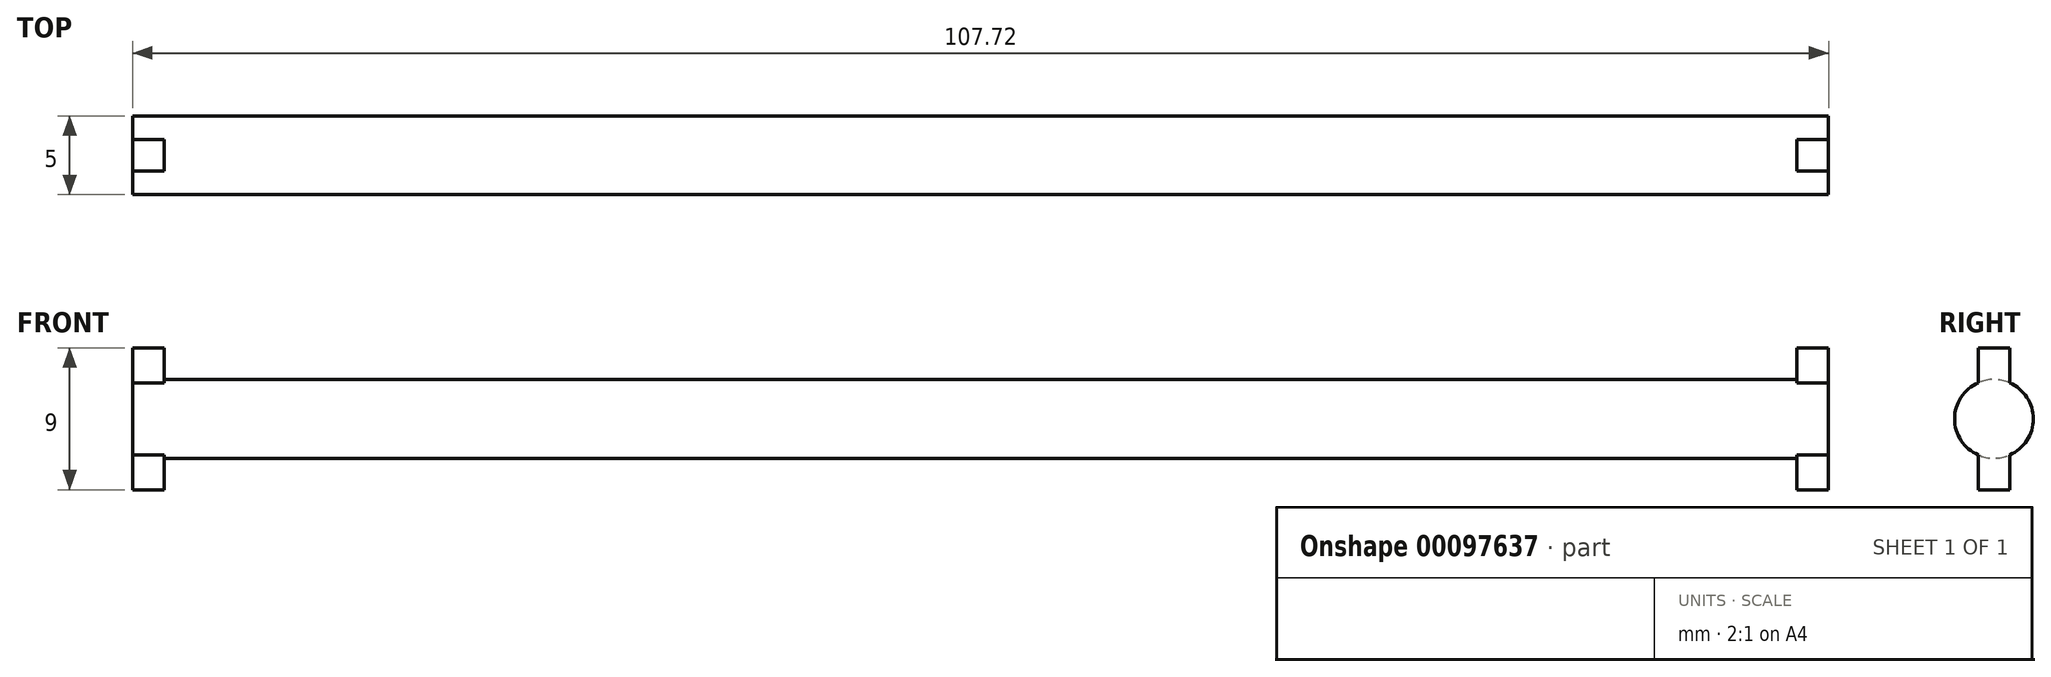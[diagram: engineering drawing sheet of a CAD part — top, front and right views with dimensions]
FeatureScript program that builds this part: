
annotation { "Feature Type Name" : "Feature", "Feature Type Description" : "" }
export const myFeature = defineFeature(function(context is Context, id is Id, definition is map)
    precondition{}
    {
        {
            var Q0;
            Q0=qCreatedBy(makeId("Right.planeOp"),FACE);
            var sketch = newSketch(context, id + "F0", { "sketchPlane" : qUnion([Q0])});
            skCircle(sketch, "E0", {"center": v(0, 0) * mm, "radius": 2.5 * mm});
            skSolve(sketch);
        }
        {
            var Q0;
            Q0=makeQuery(id+"F0.imprint","IMPRINT",FACE,{"disambiguationData":[TD([[makeQuery(id+"F0.imprint","IMPRINT",EDGE,{"derivedFrom":sQuery(id+"F0.wireOp",EDGE,"E0")}),1.0]])]});
            var Q1;
            Q1=sQuery(id+"F0.wireOp",EDGE,"E0");
            extrude(context, id + "F1", {"entities" : qUnion([Q0]), "surfaceEntities" : qUnion([Q1]), "endBound" : BoundingType.SYMMETRIC, "depth" : 107.7 * mm});
        }
        {
            var Q0;
            Q0=makeQuery(id+"F1.opExtrude","CAP_FACE",FACE,{"disambiguationData":[OSD([sQuery(id+"F0.wireOp",EDGE,"E0")])],"isStart":true});
            var sketch = newSketch(context, id + "F2", { "sketchPlane" : qUnion([Q0])});
            skLineSegment(sketch, "E1.bottom", {"start": v(1, -4.5) * mm, "end": v(-1, -4.5) * mm});
            skLineSegment(sketch, "E1.top", {"start": v(1, 4.5) * mm, "end": v(-1, 4.5) * mm});
            skLineSegment(sketch, "E1.left", {"start": v(1, -4.5) * mm, "end": v(1, 4.5) * mm});
            skLineSegment(sketch, "E1.right", {"start": v(-1, -4.5) * mm, "end": v(-1, 4.5) * mm});
            skPoint(sketch, "E1.middle", {"position": v(0, 0) * mm});
            skSolve(sketch);
        }
        {
            var Q0;
            {var subQ0=sQuery(id+"F2.wireOp",EDGE,"E1.top");Q0=makeQuery(id+"F2.imprint","IMPRINT",FACE,{"disambiguationData":[TD([[makeQuery(id+"F2.imprint","IMPRINT",EDGE,{"derivedFrom":subQ0}),1.0]])]});}
            var Q1;
            {var subQ0=sQuery(id+"F2.wireOp",EDGE,"E1.bottom");Q1=makeQuery(id+"F2.imprint","IMPRINT",FACE,{"disambiguationData":[TD([[makeQuery(id+"F2.imprint","IMPRINT",EDGE,{"derivedFrom":subQ0}),-1.0]])]});}
            extrude(context, id + "F3", {"entities" : qUnion([Q0, Q1]), "operationType" : NewBodyOperationType.ADD, "oppositeDirection" : true, "depth" : 2 * mm});
        }
        {
            var Q0;
            Q0=makeQuery(id+"F1.opExtrude","SWEPT_BODY",BODY,{"disambiguationData":[OSD([sQuery(id+"F0.wireOp",EDGE,"E0")])]});
            var Q1;
            Q1=qCreatedBy(makeId("Right.planeOp"),FACE);
            mirror(context, id + "F4", {"operationType" : NewBodyOperationType.ADD, "entities" : qUnion([Q0]), "mirrorPlane" : qUnion([Q1])});
        }
    });
